# Revit family: AtticStairs_Fakro_LSF
name_source: partatom
category: Generic Models
units: mm (PartAtom-declared; Revit-internal decimal feet)

## family parameters
Always vertical = Yes
Can host rebar = No
Cut with Voids When Loaded = No
Host = Floor
Maintain Annotation Orientation = No
Part Type = Undefined
Room Calculation Point = No
Round Connector Dimension = Use Diameter
Shared = No

## types (7) — shared parameters
zero-valued in all types: Default Elevation

## per-type parameters (varying)
| type | Box lenght | Box width | Hatch lenght | Ladder width |
| 50x70 | 700 mm  [stored 2.29659 ft] | 500 mm  [stored 1.64042 ft] | 662 mm  [stored 2.17192 ft] | 223 mm |
| 60x90 | 900 mm | 600 mm  [stored 1.9685 ft] | 862 mm | 323 mm |
| 60x120 | 1200 mm | 600 mm  [stored 1.9685 ft] | 1162 mm  [stored 3.81234 ft] | 323 mm |
| 70x80 | 800 mm  [stored 2.62467 ft] | 700 mm  [stored 2.29659 ft] | 762 mm  [stored 2.5 ft] | 423 mm |
| 70x120 | 1200 mm | 700 mm  [stored 2.29659 ft] | 1162 mm  [stored 3.81234 ft] | 423 mm |
| 70x90 | 900 mm | 700 mm  [stored 2.29659 ft] | 862 mm | 423 mm |
| 70x110 | 1100 mm | 700 mm  [stored 2.29659 ft] | 1062 mm | 423 mm |

note: [stored X ft] marks values corroborated as IEEE doubles in the binary element streams (Revit-internal decimal feet)

## geometry (parser evidence)
native form markers: Sweep x8
no freeform markers — native parametric forms only
